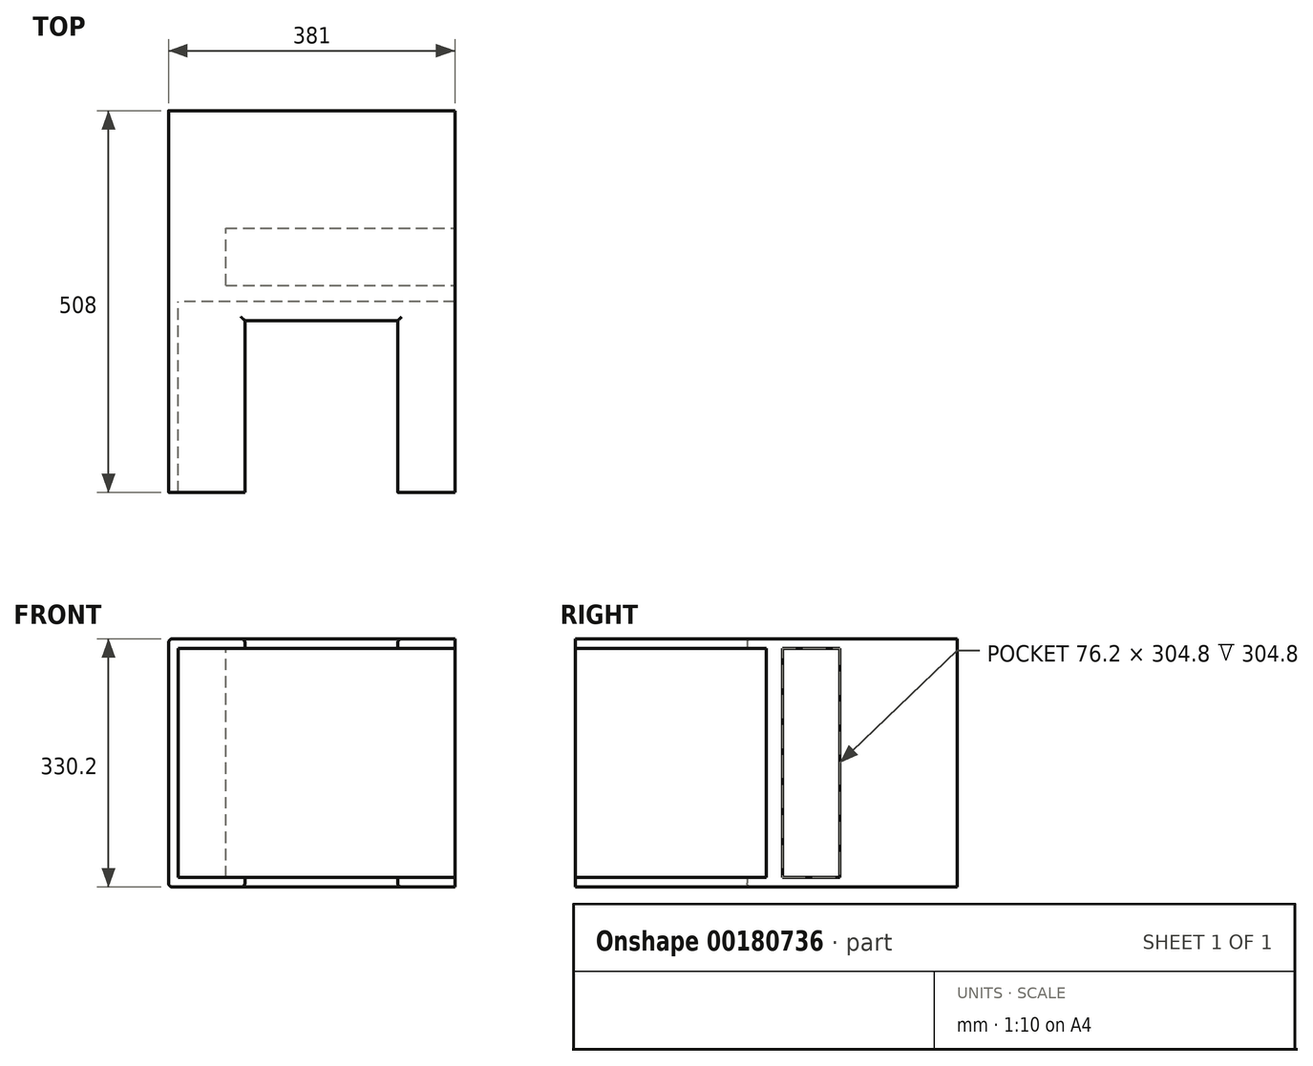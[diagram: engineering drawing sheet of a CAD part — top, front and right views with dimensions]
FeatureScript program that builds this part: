
annotation { "Feature Type Name" : "Feature", "Feature Type Description" : "" }
export const myFeature = defineFeature(function(context is Context, id is Id, definition is map)
    precondition{}
    {
        {
            var Q0;
            Q0=qCreatedBy(makeId("Front.planeOp"),FACE);
            var sketch = newSketch(context, id + "F0", { "sketchPlane" : qUnion([Q0])});
            skLineSegment(sketch, "E0", {"start": v(-171.46, 237.83) * mm, "end": v(196.84, 237.83) * mm});
            skLineSegment(sketch, "E1", {"start": v(-171.46, 237.83) * mm, "end": v(-171.46, -66.97) * mm});
            skLineSegment(sketch, "E2", {"start": v(196.84, -66.97) * mm, "end": v(-171.46, -66.97) * mm});
            skLineSegment(sketch, "E3", {"start": v(-184.16, 250.53) * mm, "end": v(196.84, 250.53) * mm});
            skLineSegment(sketch, "E4", {"start": v(-184.16, 250.53) * mm, "end": v(-184.16, -79.67) * mm});
            skLineSegment(sketch, "E5", {"start": v(-184.16, -79.67) * mm, "end": v(196.84, -79.67) * mm});
            skLineSegment(sketch, "E6", {"start": v(196.84, 250.53) * mm, "end": v(196.84, 237.83) * mm});
            skLineSegment(sketch, "E7", {"start": v(196.84, -66.97) * mm, "end": v(196.84, -79.67) * mm});
            skSolve(sketch);
        }
        {
            var Q0;
            Q0=makeQuery(id+"F0.imprint","IMPRINT",FACE,{"disambiguationData":[TD([[makeQuery(id+"F0.imprint","IMPRINT",EDGE,{"derivedFrom":sQuery(id+"F0.wireOp",EDGE,"E0")}),1.0]])]});
            extrude(context, id + "F1", {"entities" : qUnion([Q0]), "depth" : 25.4 * mm});
        }
        {
            var Q0;
            Q0=makeQuery(id+"F1.opExtrude","CAP_FACE",FACE,{"disambiguationData":[OSD([sQuery(id+"F0.wireOp",EDGE,"E0"),sQuery(id+"F0.wireOp",EDGE,"E1"),sQuery(id+"F0.wireOp",EDGE,"E2"),sQuery(id+"F0.wireOp",EDGE,"E3"),sQuery(id+"F0.wireOp",EDGE,"E4"),sQuery(id+"F0.wireOp",EDGE,"E5"),sQuery(id+"F0.wireOp",EDGE,"E6"),sQuery(id+"F0.wireOp",EDGE,"E7")])],"isStart":false});
            var sketch = newSketch(context, id + "F2", { "sketchPlane" : qUnion([Q0])});
            skLineSegment(sketch, "E8", {"start": v(-82.56, 250.53) * mm, "end": v(-82.56, 237.83) * mm});
            skLineSegment(sketch, "E9", {"start": v(-82.56, -66.97) * mm, "end": v(-82.56, -79.67) * mm});
            skLineSegment(sketch, "E10", {"start": v(120.64, 250.53) * mm, "end": v(120.64, 237.83) * mm});
            skLineSegment(sketch, "E11", {"start": v(120.64, -66.97) * mm, "end": v(120.64, -79.67) * mm});
            skSolve(sketch);
        }
        {
            var Q0;
            {var subQ5=sQuery(id+"F2.wireOp",EDGE,"E8");Q0=makeQuery(id+"F2.imprint","IMPRINT",FACE,{"disambiguationData":[TD([[makeQuery(id+"F2.imprint","IMPRINT",EDGE,{"derivedFrom":subQ5}),-1.0]])]});}
            var Q1;
            {var subQ0=sQuery(id+"F2.wireOp",EDGE,"E10");Q1=makeQuery(id+"F2.imprint","IMPRINT",FACE,{"disambiguationData":[TD([[makeQuery(id+"F2.imprint","IMPRINT",EDGE,{"derivedFrom":subQ0}),1.0]])]});}
            var Q2;
            {var subQ0=sQuery(id+"F2.wireOp",EDGE,"E11");Q2=makeQuery(id+"F2.imprint","IMPRINT",FACE,{"disambiguationData":[TD([[makeQuery(id+"F2.imprint","IMPRINT",EDGE,{"derivedFrom":subQ0}),1.0]])]});}
            extrude(context, id + "F3", {"entities" : qUnion([Q0, Q1, Q2]), "operationType" : NewBodyOperationType.ADD, "depth" : 228.6 * mm});
        }
        {
            var Q0;
            Q0=makeQuery(id+"F1.opExtrude","CAP_FACE",FACE,{"disambiguationData":[OSD([sQuery(id+"F0.wireOp",EDGE,"E0"),sQuery(id+"F0.wireOp",EDGE,"E1"),sQuery(id+"F0.wireOp",EDGE,"E2"),sQuery(id+"F0.wireOp",EDGE,"E3"),sQuery(id+"F0.wireOp",EDGE,"E4"),sQuery(id+"F0.wireOp",EDGE,"E5"),sQuery(id+"F0.wireOp",EDGE,"E6"),sQuery(id+"F0.wireOp",EDGE,"E7")])],"isStart":true});
            var sketch = newSketch(context, id + "F4", { "sketchPlane" : qUnion([Q0])});
            skLineSegment(sketch, "E12", {"start": v(-196.84, 250.53) * mm, "end": v(-196.84, -79.67) * mm});
            skSolve(sketch);
        }
        {
            var Q0;
            {var subQ1=makeQuery(id+"F1.opExtrude","CAP_EDGE",EDGE,{"disambiguationData":[OSD([sQuery(id+"F0.wireOp",EDGE,"E0")])],"isStart":true});Q0=makeQuery(id+"F4.imprint","IMPRINT",FACE,{"disambiguationData":[TD([[makeQuery(id+"F4.imprint","IMPRINT",EDGE,{"derivedFrom":subQ1}),1.0]])]});}
            var Q1;
            {var subQ3=makeQuery(id+"F1.opExtrude","CAP_EDGE",EDGE,{"disambiguationData":[OSD([sQuery(id+"F0.wireOp",EDGE,"E0")])],"isStart":true});Q1=makeQuery(id+"F4.imprint","IMPRINT",FACE,{"disambiguationData":[TD([[makeQuery(id+"F4.imprint","IMPRINT",EDGE,{"derivedFrom":subQ3}),-1.0]])]});}
            extrude(context, id + "F5", {"entities" : qUnion([Q0, Q1]), "operationType" : NewBodyOperationType.ADD, "depth" : 254 * mm});
        }
        {
            var Q0;
            {var subQ0=sQuery(id+"F0.wireOp",EDGE,"E5");var subQ1=sQuery(id+"F0.wireOp",EDGE,"E4");Q0=makeQuery(id+"F5.boolean.opBoolean","MERGE",EDGE,{"derivedFrom":[makeQuery(id+"F3.boolean.opBoolean","MERGE",EDGE,{"derivedFrom":[makeQuery(id+"F1.opExtrude","SWEPT_EDGE",EDGE,{"disambiguationData":[OSD([subQ1,subQ0])]}),makeQuery(id+"F3.opExtrude","SWEPT_EDGE",EDGE,{"disambiguationData":[OSD([subQ1,subQ0])]})]}),makeQuery(id+"F5.opExtrude","SWEPT_EDGE",EDGE,{"disambiguationData":[OSD([subQ1,subQ0])]})]});}
            var Q1;
            {var subQ0=sQuery(id+"F0.wireOp",EDGE,"E4");var subQ1=sQuery(id+"F0.wireOp",EDGE,"E3");Q1=makeQuery(id+"F5.boolean.opBoolean","MERGE",EDGE,{"derivedFrom":[makeQuery(id+"F3.boolean.opBoolean","MERGE",EDGE,{"derivedFrom":[makeQuery(id+"F1.opExtrude","SWEPT_EDGE",EDGE,{"disambiguationData":[OSD([subQ1,subQ0])]}),makeQuery(id+"F3.opExtrude","SWEPT_EDGE",EDGE,{"disambiguationData":[OSD([subQ1,subQ0])]})]}),makeQuery(id+"F5.opExtrude","SWEPT_EDGE",EDGE,{"disambiguationData":[OSD([subQ1,subQ0])]})]});}
            var Q2;
            Q2=makeQuery(id+"F3.opExtrude","SWEPT_EDGE",EDGE,{"disambiguationData":[OSD([sQuery(id+"F0.wireOp",EDGE,"E5"),sQuery(id+"F2.wireOp",EDGE,"E9")])]});
            var Q3;
            Q3=makeQuery(id+"F3.opExtrude","SWEPT_EDGE",EDGE,{"disambiguationData":[OSD([sQuery(id+"F0.wireOp",EDGE,"E5"),sQuery(id+"F2.wireOp",EDGE,"E11")])]});
            var Q4;
            Q4=makeQuery(id+"F1.opExtrude","CAP_EDGE",EDGE,{"disambiguationData":[OSD([sQuery(id+"F0.wireOp",EDGE,"E5")])],"isStart":false});
            var Q5;
            Q5=makeQuery(id+"F3.opExtrude","SWEPT_EDGE",EDGE,{"disambiguationData":[OSD([sQuery(id+"F0.wireOp",EDGE,"E3"),sQuery(id+"F2.wireOp",EDGE,"E10")])]});
            var Q6;
            Q6=makeQuery(id+"F1.opExtrude","CAP_EDGE",EDGE,{"disambiguationData":[OSD([sQuery(id+"F0.wireOp",EDGE,"E3")])],"isStart":false});
            var Q7;
            Q7=makeQuery(id+"F3.opExtrude","SWEPT_EDGE",EDGE,{"disambiguationData":[OSD([sQuery(id+"F0.wireOp",EDGE,"E3"),sQuery(id+"F2.wireOp",EDGE,"E8")])]});
            fillet(context, id + "F6", {"entities" : qUnion([Q0, Q1, Q2, Q3, Q4, Q5, Q6, Q7]), "radius" : 5.08 * mm, "tangentPropagation" : true, "allowEdgeOverflow" : false});
        }
        {
            var Q0;
            {var subQ0=sQuery(id+"F0.wireOp",EDGE,"E7");var subQ1=sQuery(id+"F0.wireOp",EDGE,"E6");Q0=makeQuery(id+"F5.boolean.opBoolean","MERGE",FACE,{"derivedFrom":[makeQuery(id+"F3.boolean.opBoolean","MERGE",FACE,{"derivedFrom":[makeQuery(id+"F1.opExtrude","SWEPT_FACE",FACE,{"disambiguationData":[OSD([subQ1])]}),makeQuery(id+"F3.opExtrude","SWEPT_FACE",FACE,{"disambiguationData":[OSD([subQ1])]})]}),makeQuery(id+"F3.boolean.opBoolean","MERGE",FACE,{"derivedFrom":[makeQuery(id+"F1.opExtrude","SWEPT_FACE",FACE,{"disambiguationData":[OSD([subQ0])]}),makeQuery(id+"F3.opExtrude","SWEPT_FACE",FACE,{"disambiguationData":[OSD([subQ0])]})]}),makeQuery(id+"F5.opExtrude","SWEPT_FACE",FACE,{"disambiguationData":[OSD([sQuery(id+"F4.wireOp",EDGE,"E12")])]})]});}
            var sketch = newSketch(context, id + "F7", { "sketchPlane" : qUnion([Q0])});
            skLineSegment(sketch, "E13", {"start": v(21.58, -66.97) * mm, "end": v(21.58, 237.83) * mm});
            skLineSegment(sketch, "E14", {"start": v(21.58, 237.83) * mm, "end": v(97.78, 237.83) * mm});
            skLineSegment(sketch, "E15", {"start": v(21.58, -66.97) * mm, "end": v(97.78, -66.97) * mm});
            skLineSegment(sketch, "E16", {"start": v(97.78, -66.97) * mm, "end": v(97.78, 237.83) * mm});
            skSolve(sketch);
        }
        {
            var Q0;
            Q0=makeQuery(id+"F7.imprint","IMPRINT",FACE,{"disambiguationData":[TD([[makeQuery(id+"F7.imprint","IMPRINT",EDGE,{"derivedFrom":sQuery(id+"F7.wireOp",EDGE,"E13")}),-1.0]])]});
            extrude(context, id + "F8", {"entities" : qUnion([Q0]), "operationType" : NewBodyOperationType.REMOVE, "oppositeDirection" : true, "depth" : 304.8 * mm});
        }
    });
